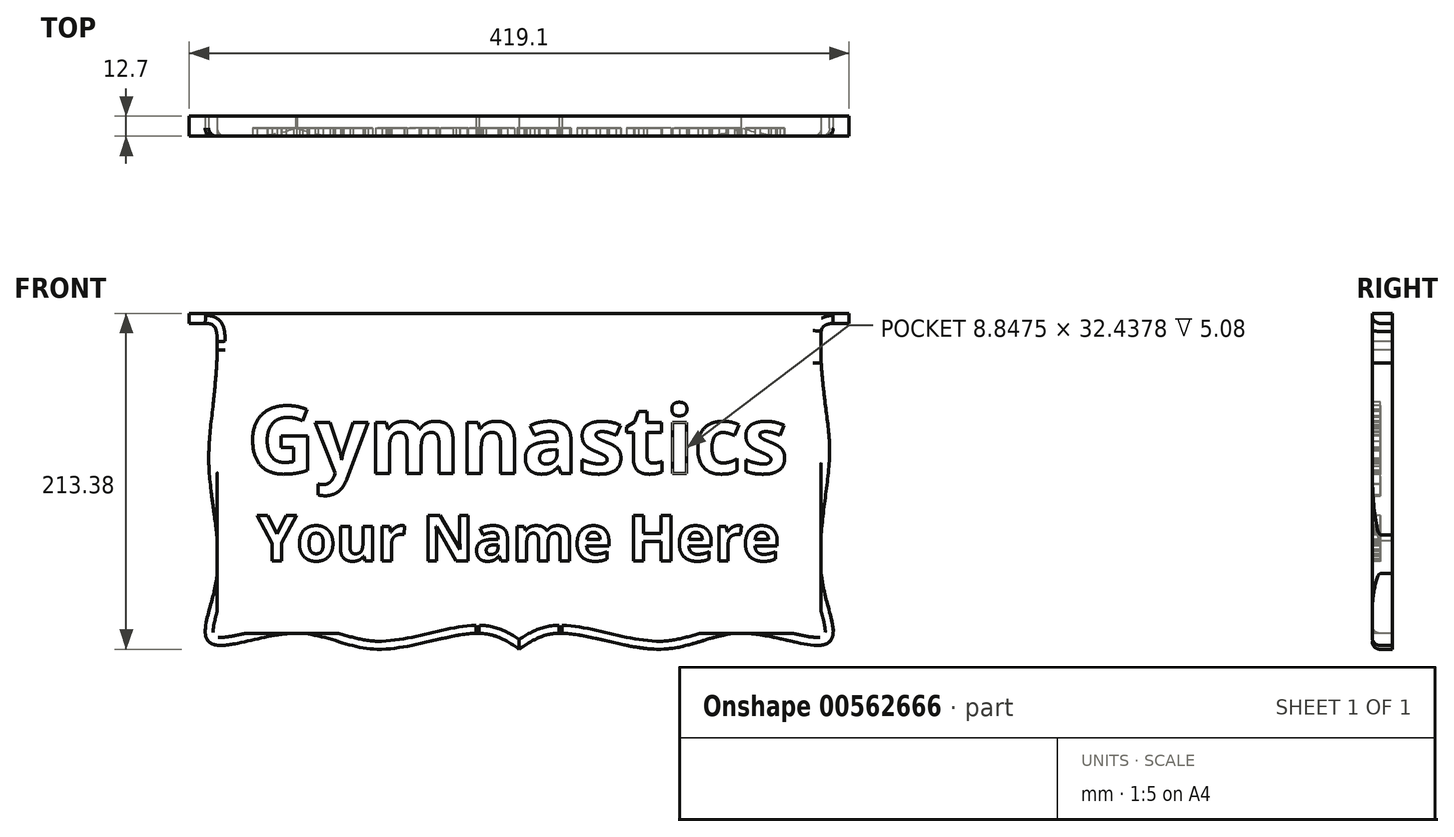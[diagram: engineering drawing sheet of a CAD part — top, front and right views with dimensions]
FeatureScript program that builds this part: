
annotation { "Feature Type Name" : "Feature", "Feature Type Description" : "" }
export const myFeature = defineFeature(function(context is Context, id is Id, definition is map)
    precondition{}
    {
        {
            var Q0;
            Q0=qCreatedBy(makeId("Front.planeOp"),FACE);
            var sketch = newSketch(context, id + "F0", { "sketchPlane" : qUnion([Q0])});
            skLineSegment(sketch, "E0.bottom", {"start": v(-209.55, 101.6) * mm, "end": v(209.55, 101.6) * mm});
            skLineSegment(sketch, "E0.top", {"start": v(-209.55, -101.6) * mm, "end": v(209.55, -101.6) * mm});
            skLineSegment(sketch, "E0.left", {"start": v(-209.55, 101.6) * mm, "end": v(-209.55, -101.6) * mm});
            skLineSegment(sketch, "E0.right", {"start": v(209.55, 101.6) * mm, "end": v(209.55, -101.6) * mm});
            skPoint(sketch, "E0.middle", {"position": v(0, 0) * mm});
            skSolve(sketch);
        }
        {
            var Q0;
            Q0=makeQuery(id+"F0.imprint","IMPRINT",FACE,{"disambiguationData":[TD([[makeQuery(id+"F0.imprint","IMPRINT",EDGE,{"derivedFrom":sQuery(id+"F0.wireOp",EDGE,"E0.bottom")}),-1.0]])]});
            extrude(context, id + "F1", {"entities" : qUnion([Q0]), "depth" : 12.7 * mm});
        }
        {
            var Q0;
            Q0=makeQuery(id+"F1.opExtrude","CAP_FACE",FACE,{"disambiguationData":[OSD([sQuery(id+"F0.wireOp",EDGE,"E0.bottom"),sQuery(id+"F0.wireOp",EDGE,"E0.top"),sQuery(id+"F0.wireOp",EDGE,"E0.left"),sQuery(id+"F0.wireOp",EDGE,"E0.right")])],"isStart":false});
            var sketch = newSketch(context, id + "F2", { "sketchPlane" : qUnion([Q0])});
            skText(sketch, "E1", { "text": "Gymnastics", "fontName": "OpenSans-Bold.ttf"});
            skText(sketch, "E2", { "text": "Your Name Here", "fontName": "OpenSans-Bold.ttf"});
            const initialGuessF2  = {"E1": [-0.17278, 0, 1, 0, 0.04278], "E2": [-0.16647, -0.05555, 1, 0, 0.02893]};
            skSetInitialGuess(sketch, initialGuessF2);
            skSolve(sketch);
        }
        {
            var Q0;
            Q0=qSketchRegion(id+"F2",true);
            extrude(context, id + "F3", {"entities" : qUnion([Q0]), "operationType" : NewBodyOperationType.REMOVE, "oppositeDirection" : true, "depth" : 5.08 * mm});
        }
        {
            var Q0;
            {var subQ0=sQuery(id+"F0.wireOp",EDGE,"E0.left");var subQ1=sQuery(id+"F0.wireOp",EDGE,"E0.bottom");var subQ2=sQuery(id+"F0.wireOp",EDGE,"E0.right");var subQ3=sQuery(id+"F0.wireOp",EDGE,"E0.top");Q0=makeQuery(id+"F3.boolean.opBoolean","SPLIT",FACE,{"disambiguationData":[TD([makeQuery(id+"F1.opExtrude","SWEPT_FACE",FACE,{"disambiguationData":[OSD([subQ1])]})])],"derivedFrom":makeQuery(id+"F1.opExtrude","CAP_FACE",FACE,{"disambiguationData":[OSD([subQ1,subQ3,subQ0,subQ2])],"isStart":false})});}
            var sketch = newSketch(context, id + "F4", { "sketchPlane" : qUnion([Q0])});
            skPoint(sketch, "E3", {"position": v(-191.77, 101.6) * mm});
            skPoint(sketch, "E4", {"position": v(-191.77, -101.6) * mm});
            skPoint(sketch, "E5", {"position": v(191.77, 101.6) * mm});
            skPoint(sketch, "E6", {"position": v(209.55, 95.25) * mm});
            skPoint(sketch, "E7", {"position": v(191.77, -101.6) * mm});
            skPoint(sketch, "E8", {"position": v(-209.55, 95.25) * mm});
            skLineSegment(sketch, "E9", {"start": v(-191.77, 101.6) * mm, "end": v(-191.77, -101.6) * mm});
            skLineSegment(sketch, "E10", {"start": v(-209.55, 95.25) * mm, "end": v(-191.77, 95.25) * mm});
            skLineSegment(sketch, "E11", {"start": v(191.77, -101.6) * mm, "end": v(191.77, 101.6) * mm});
            skLineSegment(sketch, "E12", {"start": v(209.55, 95.25) * mm, "end": v(191.77, 95.25) * mm});
            skPoint(sketch, "E13", {"position": v(-32.37, -40.44) * mm});
            skPoint(sketch, "E14", {"position": v(-37.84, -40.44) * mm});
            skSolve(sketch);
        }
        {
            var Q0;
            {var subQ3=sQuery(id+"F4.wireOp",EDGE,"E10");Q0=makeQuery(id+"F4.imprint","IMPRINT",FACE,{"disambiguationData":[TD([[makeQuery(id+"F4.imprint","IMPRINT",EDGE,{"derivedFrom":subQ3}),-1.0]])]});}
            var Q1;
            {var subQ3=sQuery(id+"F4.wireOp",EDGE,"E12");Q1=makeQuery(id+"F4.imprint","IMPRINT",FACE,{"disambiguationData":[TD([[makeQuery(id+"F4.imprint","IMPRINT",EDGE,{"derivedFrom":subQ3}),1.0]])]});}
            extrude(context, id + "F5", {"entities" : qUnion([Q0, Q1]), "operationType" : NewBodyOperationType.REMOVE, "oppositeDirection" : true, "depth" : 12.7 * mm});
        }
        {
            var Q0;
            {var subQ0=sQuery(id+"F0.wireOp",EDGE,"E0.left");var subQ1=sQuery(id+"F0.wireOp",EDGE,"E0.bottom");var subQ2=sQuery(id+"F0.wireOp",EDGE,"E0.right");var subQ3=sQuery(id+"F0.wireOp",EDGE,"E0.top");Q0=makeQuery(id+"F3.boolean.opBoolean","SPLIT",FACE,{"disambiguationData":[TD([makeQuery(id+"F1.opExtrude","SWEPT_FACE",FACE,{"disambiguationData":[OSD([subQ1])]})])],"derivedFrom":makeQuery(id+"F1.opExtrude","CAP_FACE",FACE,{"disambiguationData":[OSD([subQ1,subQ3,subQ0,subQ2])],"isStart":false})});}
            var sketch = newSketch(context, id + "F6", { "sketchPlane" : qUnion([Q0])});
            skPoint(sketch, "E15", {"position": v(-191.77, 44.45) * mm});
            skPoint(sketch, "E16", {"position": v(-191.77, 0) * mm});
            skPoint(sketch, "E17", {"position": v(-191.77, -63.5) * mm});
            skPoint(sketch, "E18", {"position": v(-140.97, -101.6) * mm});
            skPoint(sketch, "E19", {"position": v(-90.17, -101.6) * mm});
            skPoint(sketch, "E20", {"position": v(0, -101.6) * mm});
            skPoint(sketch, "E21", {"position": v(90.17, -101.6) * mm});
            skPoint(sketch, "E22", {"position": v(140.97, -101.6) * mm});
            skPoint(sketch, "E23", {"position": v(191.77, -63.5) * mm});
            skPoint(sketch, "E24", {"position": v(191.77, 6.35) * mm});
            skPoint(sketch, "E25", {"position": v(191.77, 44.45) * mm});
            skLineSegment(sketch, "E26", {"start": v(-191.77, 0) * mm, "end": v(-196.85, 0) * mm});
            skLineSegment(sketch, "E27", {"start": v(-191.77, 44.45) * mm, "end": v(-194.3, 44.45) * mm});
            skLineSegment(sketch, "E28", {"start": v(-191.77, -101.6) * mm, "end": v(-199.39, -101.6) * mm});
            skLineSegment(sketch, "E29", {"start": v(-191.77, -101.6) * mm, "end": v(-191.77, -109.22) * mm});
            skLineSegment(sketch, "E30", {"start": v(-90.17, -101.6) * mm, "end": v(-90.17, -111.76) * mm});
            skLineSegment(sketch, "E31", {"start": v(191.77, 44.45) * mm, "end": v(194.31, 44.45) * mm});
            skLineSegment(sketch, "E32", {"start": v(191.77, 6.35) * mm, "end": v(196.85, 6.35) * mm});
            skLineSegment(sketch, "E33", {"start": v(191.77, -101.6) * mm, "end": v(199.4, -101.6) * mm});
            skLineSegment(sketch, "E34", {"start": v(191.77, -101.6) * mm, "end": v(191.77, -109.22) * mm});
            skLineSegment(sketch, "E35", {"start": v(90.17, -101.6) * mm, "end": v(90.17, -111.76) * mm});
            skPoint(sketch, "E36", {"position": v(25.4, -101.6) * mm});
            skPoint(sketch, "E37", {"position": v(-25.4, -101.6) * mm});
            skLineSegment(sketch, "E38", {"start": v(0, -101.6) * mm, "end": v(0, -111.76) * mm});
            skPoint(sketch, "E39", {"position": v(199.4, 95.25) * mm});
            skPoint(sketch, "E40", {"position": v(191.77, 90.17) * mm});
            skPoint(sketch, "E41", {"position": v(194.31, 95.25) * mm});
            skLineSegment(sketch, "E42", {"start": v(194.31, 95.25) * mm, "end": v(194.31, 93.98) * mm});
            skFitSpline(sketch, "E43", {"points": [v(0, -111.76) * mm, v(25.4, -101.6) * mm, v(90.17, -111.76) * mm, v(140.97, -101.6) * mm, v(191.77, -109.22) * mm, v(199.4, -101.6) * mm, v(191.77, -63.5) * mm, v(196.85, 6.35) * mm, v(194.31, 44.45) * mm, v(191.77, 90.17) * mm, v(194.31, 93.98) * mm, v(199.4, 95.25) * mm], "startDerivative": vector(254.46, 176.78) * mm, "endDerivative": vector(162.96, 9.49) * mm});
            skPoint(sketch, "E44", {"position": v(-199.39, 95.25) * mm});
            skPoint(sketch, "E45", {"position": v(-191.77, 83.82) * mm});
            skPoint(sketch, "E46", {"position": v(-194.3, 95.25) * mm});
            skLineSegment(sketch, "E47", {"start": v(-194.3, 95.25) * mm, "end": v(-194.3, 93.98) * mm});
            skFitSpline(sketch, "E48", {"points": [v(0, -111.76) * mm, v(-25.4, -101.6) * mm, v(-90.17, -111.76) * mm, v(-140.97, -101.6) * mm, v(-191.77, -109.22) * mm, v(-199.39, -101.6) * mm, v(-191.77, -63.5) * mm, v(-196.85, 0) * mm, v(-194.3, 44.45) * mm, v(-191.77, 83.82) * mm, v(-194.3, 93.98) * mm, v(-199.39, 95.25) * mm], "startDerivative": vector(-252.39, 175.34) * mm, "endDerivative": vector(-141.61, 8.53) * mm});
            skSolve(sketch);
        }
        {
            var Q0;
            Q0=qSketchRegion(id+"F6",true);
            var Q1;
            {var subQ0=sQuery(id+"F6.wireOp",EDGE,"9e0a6239-fdb5-4647-a296-c43551efd45f");var subQ1=makeQuery(id+"F5.boolean.opBoolean","COPY",EDGE,{"derivedFrom":makeQuery(id+"F5.opExtrude","CAP_EDGE",EDGE,{"disambiguationData":[OSD([sQuery(id+"F4.wireOp",EDGE,"E11")])],"isStart":true})});var subQ2=makeQuery(id+"F6.imprint","INTERSECT",VERTEX,{"disambiguationData":[OD(0.0)],"derivedFrom":[subQ1,subQ0]});Q1=makeQuery(id+"F6.imprint","IMPRINT",FACE,{"disambiguationData":[TD([[makeQuery(id+"F6.imprint","IMPRINT",EDGE,{"disambiguationData":[TD([[subQ2,-1.0]])],"derivedFrom":subQ0}),1.0]])]});}
            var Q2;
            {var subQ0=sQuery(id+"F6.wireOp",EDGE,"d2f81a62-16b6-484c-80cf-df5878542265");var subQ1=makeQuery(id+"F5.boolean.opBoolean","COPY",EDGE,{"derivedFrom":makeQuery(id+"F5.opExtrude","CAP_EDGE",EDGE,{"disambiguationData":[OSD([sQuery(id+"F4.wireOp",EDGE,"E9")])],"isStart":true})});var subQ2=makeQuery(id+"F6.imprint","INTERSECT",VERTEX,{"disambiguationData":[OD(0.0)],"derivedFrom":[subQ1,subQ0]});Q2=makeQuery(id+"F6.imprint","IMPRINT",FACE,{"disambiguationData":[TD([[makeQuery(id+"F6.imprint","IMPRINT",EDGE,{"disambiguationData":[TD([[subQ2,-1.0]])],"derivedFrom":subQ0}),-1.0]])]});}
            var Q3;
            {var subQ0=sQuery(id+"F6.wireOp",EDGE,"E43");var subQ1=makeQuery(id+"F5.boolean.opBoolean","COPY",EDGE,{"derivedFrom":makeQuery(id+"F5.opExtrude","CAP_EDGE",EDGE,{"disambiguationData":[OSD([sQuery(id+"F4.wireOp",EDGE,"E11")])],"isStart":true})});var subQ2=makeQuery(id+"F6.imprint","INTERSECT",VERTEX,{"disambiguationData":[OD(2.0)],"derivedFrom":[subQ1,subQ0]});Q3=makeQuery(id+"F6.imprint","IMPRINT",FACE,{"disambiguationData":[TD([[makeQuery(id+"F6.imprint","IMPRINT",EDGE,{"disambiguationData":[TD([[subQ2,-1.0]])],"derivedFrom":subQ0}),-1.0]])]});}
            var Q4;
            {var subQ0=sQuery(id+"F6.wireOp",EDGE,"E48");var subQ1=makeQuery(id+"F5.boolean.opBoolean","COPY",EDGE,{"derivedFrom":makeQuery(id+"F5.opExtrude","CAP_EDGE",EDGE,{"disambiguationData":[OSD([sQuery(id+"F4.wireOp",EDGE,"E9")])],"isStart":true})});var subQ2=makeQuery(id+"F6.imprint","INTERSECT",VERTEX,{"disambiguationData":[OD(2.0)],"derivedFrom":[subQ1,subQ0]});Q4=makeQuery(id+"F6.imprint","IMPRINT",FACE,{"disambiguationData":[TD([[makeQuery(id+"F6.imprint","IMPRINT",EDGE,{"disambiguationData":[TD([[subQ2,-1.0]])],"derivedFrom":subQ0}),1.0]])]});}
            var Q5;
            {var subQ0=sQuery(id+"F6.wireOp",EDGE,"E48");var subQ1=makeQuery(id+"F5.boolean.opBoolean","COPY",EDGE,{"derivedFrom":makeQuery(id+"F5.opExtrude","CAP_EDGE",EDGE,{"disambiguationData":[OSD([sQuery(id+"F4.wireOp",EDGE,"E9")])],"isStart":true})});var subQ2=makeQuery(id+"F6.imprint","INTERSECT",VERTEX,{"disambiguationData":[OD(0.0)],"derivedFrom":[subQ1,subQ0]});Q5=makeQuery(id+"F6.imprint","IMPRINT",FACE,{"disambiguationData":[TD([[makeQuery(id+"F6.imprint","IMPRINT",EDGE,{"disambiguationData":[TD([[subQ2,-1.0]])],"derivedFrom":subQ0}),1.0]])]});}
            var Q6;
            {var subQ0=sQuery(id+"F6.wireOp",EDGE,"E43");var subQ1=makeQuery(id+"F5.boolean.opBoolean","COPY",EDGE,{"derivedFrom":makeQuery(id+"F5.opExtrude","CAP_EDGE",EDGE,{"disambiguationData":[OSD([sQuery(id+"F4.wireOp",EDGE,"E11")])],"isStart":true})});var subQ2=makeQuery(id+"F6.imprint","INTERSECT",VERTEX,{"disambiguationData":[OD(0.0)],"derivedFrom":[subQ1,subQ0]});Q6=makeQuery(id+"F6.imprint","IMPRINT",FACE,{"disambiguationData":[TD([[makeQuery(id+"F6.imprint","IMPRINT",EDGE,{"disambiguationData":[TD([[subQ2,-1.0]])],"derivedFrom":subQ0}),-1.0]])]});}
            extrude(context, id + "F7", {"entities" : qUnion([Q0, Q1, Q2, Q3, Q4, Q5, Q6]), "operationType" : NewBodyOperationType.REMOVE, "oppositeDirection" : true, "depth" : 12.7 * mm, "offsetDistance" : 25.4 * mm});
        }
        {
            var Q0;
            {var subQ0=sQuery(id+"F6.wireOp",EDGE,"E26");Q0=makeQuery(id+"F6.imprint","IMPRINT",FACE,{"disambiguationData":[TD([[makeQuery(id+"F6.imprint","IMPRINT",EDGE,{"derivedFrom":subQ0}),-1.0]])]});}
            var Q1;
            {var subQ0=sQuery(id+"F6.wireOp",EDGE,"E26");Q1=makeQuery(id+"F6.imprint","IMPRINT",FACE,{"disambiguationData":[TD([[makeQuery(id+"F6.imprint","IMPRINT",EDGE,{"derivedFrom":subQ0}),1.0]])]});}
            var Q2;
            {var subQ0=sQuery(id+"F6.wireOp",EDGE,"E27");Q2=makeQuery(id+"F6.imprint","IMPRINT",FACE,{"disambiguationData":[TD([[makeQuery(id+"F6.imprint","IMPRINT",EDGE,{"derivedFrom":subQ0}),-1.0]])]});}
            var Q3;
            {var subQ0=sQuery(id+"F6.wireOp",EDGE,"E28");Q3=makeQuery(id+"F6.imprint","IMPRINT",FACE,{"disambiguationData":[TD([[makeQuery(id+"F6.imprint","IMPRINT",EDGE,{"derivedFrom":subQ0}),-1.0]])]});}
            var Q4;
            {var subQ0=sQuery(id+"F6.wireOp",EDGE,"E28");Q4=makeQuery(id+"F6.imprint","IMPRINT",FACE,{"disambiguationData":[TD([[makeQuery(id+"F6.imprint","IMPRINT",EDGE,{"derivedFrom":subQ0}),1.0]])]});}
            var Q5;
            {var subQ0=sQuery(id+"F6.wireOp",EDGE,"E29");Q5=makeQuery(id+"F6.imprint","IMPRINT",FACE,{"disambiguationData":[TD([[makeQuery(id+"F6.imprint","IMPRINT",EDGE,{"derivedFrom":subQ0}),1.0]])]});}
            var Q6;
            {var subQ0=sQuery(id+"F6.wireOp",EDGE,"E30");Q6=makeQuery(id+"F6.imprint","IMPRINT",FACE,{"disambiguationData":[TD([[makeQuery(id+"F6.imprint","IMPRINT",EDGE,{"derivedFrom":subQ0}),-1.0]])]});}
            var Q7;
            {var subQ0=sQuery(id+"F6.wireOp",EDGE,"E30");Q7=makeQuery(id+"F6.imprint","IMPRINT",FACE,{"disambiguationData":[TD([[makeQuery(id+"F6.imprint","IMPRINT",EDGE,{"derivedFrom":subQ0}),1.0]])]});}
            var Q8;
            {var subQ0=sQuery(id+"F6.wireOp",EDGE,"E38");Q8=makeQuery(id+"F6.imprint","IMPRINT",FACE,{"disambiguationData":[TD([[makeQuery(id+"F6.imprint","IMPRINT",EDGE,{"derivedFrom":subQ0}),-1.0]])]});}
            var Q9;
            {var subQ0=sQuery(id+"F6.wireOp",EDGE,"E38");Q9=makeQuery(id+"F6.imprint","IMPRINT",FACE,{"disambiguationData":[TD([[makeQuery(id+"F6.imprint","IMPRINT",EDGE,{"derivedFrom":subQ0}),1.0]])]});}
            var Q10;
            {var subQ0=sQuery(id+"F6.wireOp",EDGE,"9e0a6239-fdb5-4647-a296-c43551efd45f");var subQ1=sQuery(id+"F6.wireOp",EDGE,"E35");var subQ2=makeQuery(id+"F6.imprint","INTERSECT",VERTEX,{"derivedFrom":[subQ1,subQ0]});Q10=makeQuery(id+"F6.imprint","IMPRINT",FACE,{"disambiguationData":[TD([[makeQuery(id+"F6.imprint","IMPRINT",EDGE,{"disambiguationData":[TD([[subQ2,1.0]])],"derivedFrom":subQ1}),-1.0]])]});}
            var Q11;
            {var subQ0=sQuery(id+"F6.wireOp",EDGE,"9e0a6239-fdb5-4647-a296-c43551efd45f");var subQ1=sQuery(id+"F6.wireOp",EDGE,"E35");var subQ2=makeQuery(id+"F6.imprint","INTERSECT",VERTEX,{"derivedFrom":[subQ1,subQ0]});Q11=makeQuery(id+"F6.imprint","IMPRINT",FACE,{"disambiguationData":[TD([[makeQuery(id+"F6.imprint","IMPRINT",EDGE,{"disambiguationData":[TD([[subQ2,1.0]])],"derivedFrom":subQ1}),1.0]])]});}
            var Q12;
            {var subQ0=sQuery(id+"F6.wireOp",EDGE,"E34");Q12=makeQuery(id+"F6.imprint","IMPRINT",FACE,{"disambiguationData":[TD([[makeQuery(id+"F6.imprint","IMPRINT",EDGE,{"derivedFrom":subQ0}),-1.0]])]});}
            var Q13;
            {var subQ0=sQuery(id+"F6.wireOp",EDGE,"E33");Q13=makeQuery(id+"F6.imprint","IMPRINT",FACE,{"disambiguationData":[TD([[makeQuery(id+"F6.imprint","IMPRINT",EDGE,{"derivedFrom":subQ0}),-1.0]])]});}
            var Q14;
            {var subQ0=sQuery(id+"F6.wireOp",EDGE,"E33");Q14=makeQuery(id+"F6.imprint","IMPRINT",FACE,{"disambiguationData":[TD([[makeQuery(id+"F6.imprint","IMPRINT",EDGE,{"derivedFrom":subQ0}),1.0]])]});}
            var Q15;
            {var subQ0=sQuery(id+"F6.wireOp",EDGE,"E32");Q15=makeQuery(id+"F6.imprint","IMPRINT",FACE,{"disambiguationData":[TD([[makeQuery(id+"F6.imprint","IMPRINT",EDGE,{"derivedFrom":subQ0}),-1.0]])]});}
            var Q16;
            {var subQ0=sQuery(id+"F6.wireOp",EDGE,"E31");Q16=makeQuery(id+"F6.imprint","IMPRINT",FACE,{"disambiguationData":[TD([[makeQuery(id+"F6.imprint","IMPRINT",EDGE,{"derivedFrom":subQ0}),-1.0]])]});}
            var Q17;
            {var subQ0=sQuery(id+"F6.wireOp",EDGE,"E31");Q17=makeQuery(id+"F6.imprint","IMPRINT",FACE,{"disambiguationData":[TD([[makeQuery(id+"F6.imprint","IMPRINT",EDGE,{"derivedFrom":subQ0}),1.0]])]});}
            var Q18;
            {var subQ0=sQuery(id+"F6.wireOp",EDGE,"9e0a6239-fdb5-4647-a296-c43551efd45f");var subQ1=makeQuery(id+"F6.imprint","IMPRINT",VERTEX,{"derivedFrom":subQ0});Q18=makeQuery(id+"F6.imprint","IMPRINT",FACE,{"disambiguationData":[TD([[makeQuery(id+"F6.imprint","IMPRINT",EDGE,{"disambiguationData":[TD([[subQ1,1.0]])],"derivedFrom":subQ0}),-1.0]])]});}
            var Q19;
            {var subQ0=sQuery(id+"F6.wireOp",EDGE,"E42");Q19=makeQuery(id+"F6.imprint","IMPRINT",FACE,{"disambiguationData":[TD([[makeQuery(id+"F6.imprint","IMPRINT",EDGE,{"derivedFrom":subQ0}),-1.0]])]});}
            var Q20;
            {var subQ0=sQuery(id+"F6.wireOp",EDGE,"E42");Q20=makeQuery(id+"F6.imprint","IMPRINT",FACE,{"disambiguationData":[TD([[makeQuery(id+"F6.imprint","IMPRINT",EDGE,{"derivedFrom":subQ0}),1.0]])]});}
            var Q21;
            {var subQ0=sQuery(id+"F6.wireOp",EDGE,"E47");Q21=makeQuery(id+"F6.imprint","IMPRINT",FACE,{"disambiguationData":[TD([[makeQuery(id+"F6.imprint","IMPRINT",EDGE,{"derivedFrom":subQ0}),1.0]])]});}
            var Q22;
            {var subQ0=sQuery(id+"F6.wireOp",EDGE,"E47");Q22=makeQuery(id+"F6.imprint","IMPRINT",FACE,{"disambiguationData":[TD([[makeQuery(id+"F6.imprint","IMPRINT",EDGE,{"derivedFrom":subQ0}),-1.0]])]});}
            extrude(context, id + "F8", {"entities" : qUnion([Q0, Q1, Q2, Q3, Q4, Q5, Q6, Q7, Q8, Q9, Q10, Q11, Q12, Q13, Q14, Q15, Q16, Q17, Q18, Q19, Q20, Q21, Q22]), "operationType" : NewBodyOperationType.ADD, "depth" : -12.7 * mm, "offsetDistance" : 25.4 * mm});
        }
        {
            var Q0;
            {var subQ0=sQuery(id+"F6.wireOp",EDGE,"E48");var subQ1=makeQuery(id+"F6.imprint","INTERSECT",VERTEX,{"derivedFrom":[sQuery(id+"F6.wireOp",EDGE,"E47"),subQ0]});var subQ2=makeQuery(id+"F5.boolean.opBoolean","COPY",EDGE,{"derivedFrom":makeQuery(id+"F5.opExtrude","CAP_EDGE",EDGE,{"disambiguationData":[OSD([sQuery(id+"F4.wireOp",EDGE,"E9")])],"isStart":true})});var subQ4=makeQuery(id+"F6.imprint","INTERSECT",VERTEX,{"derivedFrom":[sQuery(id+"F6.wireOp",EDGE,"E27"),subQ0]});var subQ5=makeQuery(id+"F6.imprint","INTERSECT",VERTEX,{"disambiguationData":[OD(2.0)],"derivedFrom":[subQ2,subQ0]});var subQ6=makeQuery(id+"F6.imprint","INTERSECT",VERTEX,{"derivedFrom":[sQuery(id+"F6.wireOp",EDGE,"E26"),subQ0]});var subQ8=makeQuery(id+"F6.imprint","INTERSECT",VERTEX,{"derivedFrom":[sQuery(id+"F6.wireOp",EDGE,"E28"),subQ0]});var subQ9=makeQuery(id+"F6.imprint","INTERSECT",VERTEX,{"disambiguationData":[OD(0.0)],"derivedFrom":[subQ2,subQ0]});var subQ10=makeQuery(id+"F6.imprint","INTERSECT",VERTEX,{"derivedFrom":[sQuery(id+"F6.wireOp",EDGE,"E29"),subQ0]});Q0=makeQuery(id+"F8.boolean.opBoolean","MERGE",EDGE,{"derivedFrom":[makeQuery(id+"F7.boolean.opBoolean","COPY",EDGE,{"derivedFrom":makeQuery(id+"F7.opExtrude","CAP_EDGE",EDGE,{"disambiguationData":[OSD([subQ0]),TDD([makeQuery(id+"F6.imprint","IMPRINT",EDGE,{"disambiguationData":[TD([[subQ9,-1.0]])],"derivedFrom":subQ0})])],"isStart":true})}),makeQuery(id+"F7.boolean.opBoolean","COPY",EDGE,{"derivedFrom":makeQuery(id+"F7.opExtrude","CAP_EDGE",EDGE,{"disambiguationData":[OSD([subQ0]),TDD([makeQuery(id+"F6.imprint","IMPRINT",EDGE,{"disambiguationData":[TD([[subQ5,-1.0]])],"derivedFrom":subQ0})])],"isStart":true})}),makeQuery(id+"F8.opExtrude","CAP_EDGE",EDGE,{"disambiguationData":[OSD([subQ0]),TDD([makeQuery(id+"F6.imprint","IMPRINT",EDGE,{"disambiguationData":[TD([[subQ10,1.0]])],"derivedFrom":subQ0}),makeQuery(id+"F6.imprint","IMPRINT",EDGE,{"disambiguationData":[TD([[subQ8,1.0]])],"derivedFrom":subQ0}),makeQuery(id+"F6.imprint","IMPRINT",EDGE,{"disambiguationData":[TD([[subQ8,-1.0]])],"derivedFrom":subQ0})])],"isStart":true}),makeQuery(id+"F8.opExtrude","CAP_EDGE",EDGE,{"disambiguationData":[OSD([subQ0]),TDD([makeQuery(id+"F6.imprint","IMPRINT",EDGE,{"disambiguationData":[TD([[subQ6,1.0]])],"derivedFrom":subQ0}),makeQuery(id+"F6.imprint","IMPRINT",EDGE,{"disambiguationData":[TD([[subQ6,-1.0]])],"derivedFrom":subQ0}),makeQuery(id+"F6.imprint","IMPRINT",EDGE,{"disambiguationData":[TD([[subQ4,-1.0]])],"derivedFrom":subQ0})])],"isStart":true}),makeQuery(id+"F8.opExtrude","CAP_EDGE",EDGE,{"disambiguationData":[OSD([subQ0]),TDD([makeQuery(id+"F6.imprint","IMPRINT",EDGE,{"disambiguationData":[TD([[subQ1,1.0]])],"derivedFrom":subQ0}),makeQuery(id+"F6.imprint","IMPRINT",EDGE,{"disambiguationData":[TD([[subQ1,-1.0]])],"derivedFrom":subQ0})])],"isStart":true})]});}
            var Q1;
            {var subQ0=sQuery(id+"F6.wireOp",EDGE,"E48");var subQ1=makeQuery(id+"F6.imprint","INTERSECT",VERTEX,{"derivedFrom":[sQuery(id+"F6.wireOp",EDGE,"E30"),subQ0]});Q1=makeQuery(id+"F8.opExtrude","CAP_EDGE",EDGE,{"disambiguationData":[OSD([subQ0]),TDD([makeQuery(id+"F6.imprint","IMPRINT",EDGE,{"disambiguationData":[TD([[subQ1,1.0]])],"derivedFrom":subQ0}),makeQuery(id+"F6.imprint","IMPRINT",EDGE,{"disambiguationData":[TD([[subQ1,-1.0]])],"derivedFrom":subQ0})])],"isStart":true});}
            var Q2;
            {var subQ0=sQuery(id+"F6.wireOp",EDGE,"E48");Q2=makeQuery(id+"F8.opExtrude","CAP_EDGE",EDGE,{"disambiguationData":[OSD([subQ0]),TDD([makeQuery(id+"F6.imprint","IMPRINT",EDGE,{"disambiguationData":[TD([[makeQuery(id+"F6.imprint","INTERSECT",VERTEX,{"disambiguationData":[OD(0.0)],"derivedFrom":[makeQuery(id+"F1.opExtrude","CAP_EDGE",EDGE,{"disambiguationData":[OSD([sQuery(id+"F0.wireOp",EDGE,"E0.top")])],"isStart":false}),subQ0]}),1.0]])],"derivedFrom":subQ0})])],"isStart":true});}
            var Q3;
            {var subQ0=sQuery(id+"F6.wireOp",EDGE,"E43");Q3=makeQuery(id+"F8.opExtrude","CAP_EDGE",EDGE,{"disambiguationData":[OSD([subQ0]),TDD([makeQuery(id+"F6.imprint","IMPRINT",EDGE,{"disambiguationData":[TD([[makeQuery(id+"F6.imprint","INTERSECT",VERTEX,{"disambiguationData":[OD(0.0)],"derivedFrom":[makeQuery(id+"F1.opExtrude","CAP_EDGE",EDGE,{"disambiguationData":[OSD([sQuery(id+"F0.wireOp",EDGE,"E0.top")])],"isStart":false}),subQ0]}),1.0]])],"derivedFrom":subQ0})])],"isStart":true});}
            var Q4;
            {var subQ0=sQuery(id+"F6.wireOp",EDGE,"E43");var subQ1=makeQuery(id+"F6.imprint","INTERSECT",VERTEX,{"derivedFrom":[sQuery(id+"F6.wireOp",EDGE,"E35"),subQ0]});Q4=makeQuery(id+"F8.opExtrude","CAP_EDGE",EDGE,{"disambiguationData":[OSD([subQ0]),TDD([makeQuery(id+"F6.imprint","IMPRINT",EDGE,{"disambiguationData":[TD([[subQ1,1.0]])],"derivedFrom":subQ0}),makeQuery(id+"F6.imprint","IMPRINT",EDGE,{"disambiguationData":[TD([[subQ1,-1.0]])],"derivedFrom":subQ0})])],"isStart":true});}
            var Q5;
            {var subQ0=sQuery(id+"F6.wireOp",EDGE,"E43");var subQ1=makeQuery(id+"F6.imprint","INTERSECT",VERTEX,{"derivedFrom":[sQuery(id+"F6.wireOp",EDGE,"E42"),subQ0]});var subQ2=makeQuery(id+"F5.boolean.opBoolean","COPY",EDGE,{"derivedFrom":makeQuery(id+"F5.opExtrude","CAP_EDGE",EDGE,{"disambiguationData":[OSD([sQuery(id+"F4.wireOp",EDGE,"E11")])],"isStart":true})});var subQ4=makeQuery(id+"F6.imprint","INTERSECT",VERTEX,{"derivedFrom":[sQuery(id+"F6.wireOp",EDGE,"E31"),subQ0]});var subQ5=makeQuery(id+"F6.imprint","INTERSECT",VERTEX,{"disambiguationData":[OD(2.0)],"derivedFrom":[subQ2,subQ0]});var subQ6=makeQuery(id+"F6.imprint","INTERSECT",VERTEX,{"derivedFrom":[sQuery(id+"F6.wireOp",EDGE,"E32"),subQ0]});var subQ8=makeQuery(id+"F6.imprint","INTERSECT",VERTEX,{"derivedFrom":[sQuery(id+"F6.wireOp",EDGE,"E33"),subQ0]});var subQ9=makeQuery(id+"F6.imprint","INTERSECT",VERTEX,{"disambiguationData":[OD(0.0)],"derivedFrom":[subQ2,subQ0]});var subQ10=makeQuery(id+"F6.imprint","INTERSECT",VERTEX,{"derivedFrom":[sQuery(id+"F6.wireOp",EDGE,"E34"),subQ0]});Q5=makeQuery(id+"F8.boolean.opBoolean","MERGE",EDGE,{"derivedFrom":[makeQuery(id+"F7.boolean.opBoolean","COPY",EDGE,{"derivedFrom":makeQuery(id+"F7.opExtrude","CAP_EDGE",EDGE,{"disambiguationData":[OSD([subQ0]),TDD([makeQuery(id+"F6.imprint","IMPRINT",EDGE,{"disambiguationData":[TD([[subQ9,-1.0]])],"derivedFrom":subQ0})])],"isStart":true})}),makeQuery(id+"F7.boolean.opBoolean","COPY",EDGE,{"derivedFrom":makeQuery(id+"F7.opExtrude","CAP_EDGE",EDGE,{"disambiguationData":[OSD([subQ0]),TDD([makeQuery(id+"F6.imprint","IMPRINT",EDGE,{"disambiguationData":[TD([[subQ5,-1.0]])],"derivedFrom":subQ0})])],"isStart":true})}),makeQuery(id+"F8.opExtrude","CAP_EDGE",EDGE,{"disambiguationData":[OSD([subQ0]),TDD([makeQuery(id+"F6.imprint","IMPRINT",EDGE,{"disambiguationData":[TD([[subQ10,1.0]])],"derivedFrom":subQ0}),makeQuery(id+"F6.imprint","IMPRINT",EDGE,{"disambiguationData":[TD([[subQ8,1.0]])],"derivedFrom":subQ0}),makeQuery(id+"F6.imprint","IMPRINT",EDGE,{"disambiguationData":[TD([[subQ8,-1.0]])],"derivedFrom":subQ0})])],"isStart":true}),makeQuery(id+"F8.opExtrude","CAP_EDGE",EDGE,{"disambiguationData":[OSD([subQ0]),TDD([makeQuery(id+"F6.imprint","IMPRINT",EDGE,{"disambiguationData":[TD([[subQ6,1.0]])],"derivedFrom":subQ0}),makeQuery(id+"F6.imprint","IMPRINT",EDGE,{"disambiguationData":[TD([[subQ4,1.0]])],"derivedFrom":subQ0}),makeQuery(id+"F6.imprint","IMPRINT",EDGE,{"disambiguationData":[TD([[subQ4,-1.0]])],"derivedFrom":subQ0})])],"isStart":true}),makeQuery(id+"F8.opExtrude","CAP_EDGE",EDGE,{"disambiguationData":[OSD([subQ0]),TDD([makeQuery(id+"F6.imprint","IMPRINT",EDGE,{"disambiguationData":[TD([[subQ1,1.0]])],"derivedFrom":subQ0}),makeQuery(id+"F6.imprint","IMPRINT",EDGE,{"disambiguationData":[TD([[subQ1,-1.0]])],"derivedFrom":subQ0})])],"isStart":true})]});}
            var Q6;
            {var subQ2=sQuery(id+"F0.wireOp",EDGE,"E0.top");var subQ3=sQuery(id+"F6.wireOp",EDGE,"E48");var subQ5=makeQuery(id+"F1.opExtrude","CAP_EDGE",EDGE,{"disambiguationData":[OSD([subQ2])],"isStart":false});var subQ6=sQuery(id+"F4.wireOp",EDGE,"E9");var subQ7=makeQuery(id+"F5.boolean.opBoolean","COPY",EDGE,{"derivedFrom":makeQuery(id+"F5.opExtrude","CAP_EDGE",EDGE,{"disambiguationData":[OSD([subQ6])],"isStart":true})});var subQ8=makeQuery(id+"F6.imprint","INTERSECT",VERTEX,{"disambiguationData":[OD(0.0)],"derivedFrom":[subQ7,subQ3]});Q6=makeQuery(id+"F8.boolean.opBoolean","SPLIT",EDGE,{"disambiguationData":[TD([makeQuery(id+"F7.boolean.opBoolean","COPY",FACE,{"derivedFrom":makeQuery(id+"F7.opExtrude","SWEPT_FACE",FACE,{"disambiguationData":[OSD([subQ3]),TDD([makeQuery(id+"F6.imprint","IMPRINT",EDGE,{"disambiguationData":[TD([[subQ8,-1.0]])],"derivedFrom":subQ3})])]})})])],"derivedFrom":subQ5});}
            var Q7;
            {var subQ2=sQuery(id+"F0.wireOp",EDGE,"E0.top");var subQ3=sQuery(id+"F6.wireOp",EDGE,"E48");var subQ5=makeQuery(id+"F1.opExtrude","CAP_EDGE",EDGE,{"disambiguationData":[OSD([subQ2])],"isStart":false});Q7=makeQuery(id+"F8.boolean.opBoolean","SPLIT",EDGE,{"disambiguationData":[TD([makeQuery(id+"F8.opExtrude","SWEPT_FACE",FACE,{"disambiguationData":[OSD([subQ3]),TDD([makeQuery(id+"F6.imprint","IMPRINT",EDGE,{"disambiguationData":[TD([[makeQuery(id+"F6.imprint","INTERSECT",VERTEX,{"disambiguationData":[OD(0.0)],"derivedFrom":[subQ5,subQ3]}),1.0]])],"derivedFrom":subQ3})])]})])],"derivedFrom":subQ5});}
            var Q8;
            {var subQ0=sQuery(id+"F6.wireOp",EDGE,"E43");var subQ2=sQuery(id+"F0.wireOp",EDGE,"E0.top");var subQ4=makeQuery(id+"F1.opExtrude","CAP_EDGE",EDGE,{"disambiguationData":[OSD([subQ2])],"isStart":false});Q8=makeQuery(id+"F8.boolean.opBoolean","SPLIT",EDGE,{"disambiguationData":[TD([makeQuery(id+"F8.opExtrude","SWEPT_FACE",FACE,{"disambiguationData":[OSD([subQ0]),TDD([makeQuery(id+"F6.imprint","IMPRINT",EDGE,{"disambiguationData":[TD([[makeQuery(id+"F6.imprint","INTERSECT",VERTEX,{"disambiguationData":[OD(0.0)],"derivedFrom":[subQ4,subQ0]}),1.0]])],"derivedFrom":subQ0})])]})])],"derivedFrom":subQ4});}
            var Q9;
            {var subQ0=sQuery(id+"F6.wireOp",EDGE,"E43");var subQ2=sQuery(id+"F4.wireOp",EDGE,"E11");var subQ3=makeQuery(id+"F5.boolean.opBoolean","COPY",EDGE,{"derivedFrom":makeQuery(id+"F5.opExtrude","CAP_EDGE",EDGE,{"disambiguationData":[OSD([subQ2])],"isStart":true})});var subQ7=sQuery(id+"F0.wireOp",EDGE,"E0.top");var subQ9=makeQuery(id+"F1.opExtrude","CAP_EDGE",EDGE,{"disambiguationData":[OSD([subQ7])],"isStart":false});var subQ12=makeQuery(id+"F6.imprint","INTERSECT",VERTEX,{"disambiguationData":[OD(0.0)],"derivedFrom":[subQ3,subQ0]});Q9=makeQuery(id+"F8.boolean.opBoolean","SPLIT",EDGE,{"disambiguationData":[TD([makeQuery(id+"F7.boolean.opBoolean","COPY",FACE,{"derivedFrom":makeQuery(id+"F7.opExtrude","SWEPT_FACE",FACE,{"disambiguationData":[OSD([subQ0]),TDD([makeQuery(id+"F6.imprint","IMPRINT",EDGE,{"disambiguationData":[TD([[subQ12,-1.0]])],"derivedFrom":subQ0})])]})})])],"derivedFrom":subQ9});}
            fillet(context, id + "F9", {"entities" : qUnion([Q0, Q1, Q2, Q3, Q4, Q5, Q6, Q7, Q8, Q9]), "radius" : 5.08 * mm, "tangentPropagation" : true, "allowEdgeOverflow" : false});
        }
    });
